# Revit family: LTDCR4X4
name_source: partatom
category: Lighting Fixtures
units: mm (PartAtom-declared; Revit-internal decimal feet)

## family parameters
Always vertical = Yes
Cut with Voids When Loaded = No
Host = Ceiling
Light Source = Yes
Maintain Annotation Orientation = No
OmniClass Number = 23.80.70.11
OmniClass Title = Luminaries for Internal Lighting
Part Type = Normal
Room Calculation Point = No
Round Connector Dimension = Use Diameter
Shared = No

## types (2) — shared parameters
Assembly Code = D5020200
Color Filter = 16777215
Default Elevation = 0' - 0"
Description = Click image to enlarge
LED Troffer Dish Circular Recessed
Dimming Lamp Color Temperature Shift = <None>
Emit Shape Visible in Rendering = No
Emit from Rectangle Length = 3' - 10 3/4"
Emit from Rectangle Width = 3' - 10 3/4"
Housing Finish = Metal - Viscor - White
Lamp = LED
Length = 3' - 10 3/4"
Lens Finish = Polycarbonate - Viscor - Frosted Round
Manufacturer = Visioneering of VISCOR
Model = LTDCR-XL
Tilt Angle = 90.00°
URL = https://viscor.com
Voltage = 120 V
Width = 3' - 10 3/4"

## per-type parameters (varying)
| type | Apparent Load | Lamp Wattage | Photometric Web File |
| LTDCR4X4-LED840K070LUNV | 67 VA | 67 VA | LTDCR4X4-LED840K-070LUNV.ies |
| LTDCR4X4-LED840K105LUNV | 103 VA | 103 VA | LTDCR4X4-LED840K-105LUNV.ies |

## geometry (parser evidence)
native form markers: Sweep x3
no freeform markers — native parametric forms only
